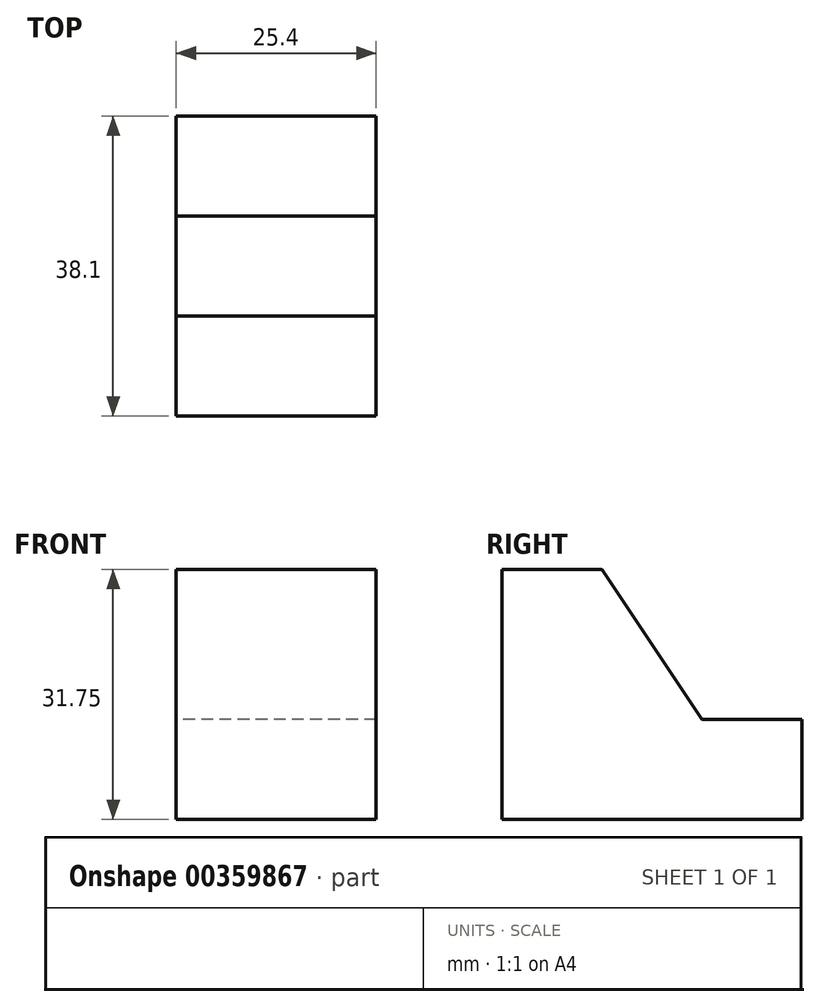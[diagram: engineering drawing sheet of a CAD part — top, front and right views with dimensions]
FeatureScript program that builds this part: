
annotation { "Feature Type Name" : "Feature", "Feature Type Description" : "" }
export const myFeature = defineFeature(function(context is Context, id is Id, definition is map)
    precondition{}
    {
        {
            var Q0;
            Q0=qCreatedBy(makeId("Right.planeOp"),FACE);
            var sketch = newSketch(context, id + "F0", { "sketchPlane" : qUnion([Q0])});
            skLineSegment(sketch, "E0", {"start": v(0, 0) * mm, "end": v(38.1, 0) * mm});
            skLineSegment(sketch, "E1", {"start": v(38.1, 0) * mm, "end": v(38.1, 12.7) * mm});
            skLineSegment(sketch, "E2", {"start": v(38.1, 12.7) * mm, "end": v(25.4, 12.7) * mm});
            skLineSegment(sketch, "E3", {"start": v(25.4, 12.7) * mm, "end": v(12.7, 31.75) * mm});
            skLineSegment(sketch, "E4", {"start": v(12.7, 31.75) * mm, "end": v(0, 31.75) * mm});
            skLineSegment(sketch, "E5", {"start": v(0, 31.75) * mm, "end": v(0, 0) * mm});
            skSolve(sketch);
        }
        {
            var Q0;
            Q0=makeQuery(id+"F0.imprint","IMPRINT",FACE,{"disambiguationData":[TD([[makeQuery(id+"F0.imprint","IMPRINT",EDGE,{"derivedFrom":sQuery(id+"F0.wireOp",EDGE,"E0")}),1.0]])]});
            extrude(context, id + "F1", {"entities" : qUnion([Q0]), "depth" : 25.4 * mm});
        }
    });
